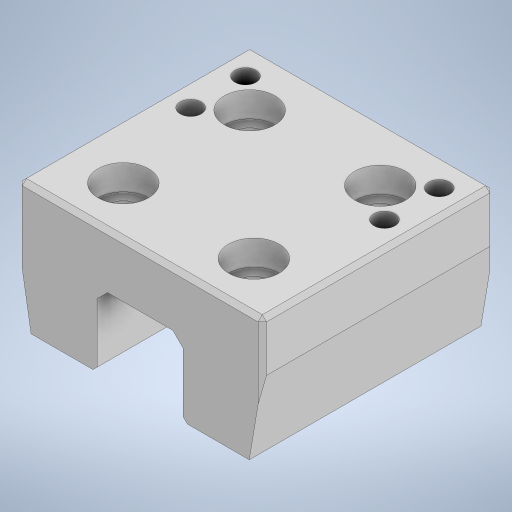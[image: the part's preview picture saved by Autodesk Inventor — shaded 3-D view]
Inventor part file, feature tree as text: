
AUTODESK INVENTOR PART (.ipt)
format: ipt  version: 2023 (Build 270158000, 158)  size: 463,872 bytes
history: native  units: in
note: dims shown in document units (in); Inventor stores cm internally (conversion verified against a paired STEP export)
features: extrude x11, sketch x7, projected_geometry x3, chamfer x2, thicken_offset x1
ambient origin geometry x8: Origin, YZ Plane, XZ Plane, XY Plane, X Axis, Y Axis, Z Axis, Center Point
bodies: Solid1 (feature_tree)
feature tree (24):
  extrude  "Extrusion1"  Depth=2.3622in
  extrude  "Extrusion2"  Depth=0.0197in
  extrude  "Extrusion3"  Depth=0.0197in
  extrude  "Extrusion4"  Depth=0.1969in
  extrude  "Extrusion5"  Depth=2.7874in
  extrude  "Extrusion6"  Depth=2.1654in TaperAngle=0.0deg
  extrude  "Extrusion9"  Depth=0.3937in TaperAngle=0.0deg
  extrude  "Extrusion10"  Depth=0.3937in TaperAngle=0.0deg
  extrude  "Extrusion11"  Depth=0.1969in
  extrude  "Extrusion12"  Depth=0.1969in TaperAngle=0.0deg
  extrude  "Extrusion13"  Depth=0.1969in
  chamfer  "Chamfer2"  Distance=0.2362in
  thicken_offset  "Thicken1"
  chamfer  "Chamfer1"  Distance=1.3937in
  sketch  "Sketch4"  dims[d0=0.9843in d1=2.3622in]
  sketch  "Sketch5"  dims[d2=0.0197in d3=0.0197in]
  sketch  "Sketch8"  dims[d4=0.0197in d5=0.0197in]
  sketch  "Sketch10"  dims[d6=0.1969in d7=1.811in]
  projected_geometry  "Projected Loop1"
  sketch  "Sketch11"  dims[d8=0.5118in d9=2.7874in]
  sketch  "Sketch12"  dims[d10=2.1654in d11=1.3937in d12=0.0in]
  sketch  "Sketch13"  dims[d13=1.3937in d14=0.0in d15=0.3937in d16=0.1969in d17=0.0in d18=0.0in d19=0.3937in d20=1.1969in d21=0.0in d22=0.0in d27=0.3937in d28=0.0in d29=0.2687in d31=1.4375in d32=0.0in d34=0.4724in d35=0.2362in d36=0.0in d50=1.3937in d51=0.0394in d52=0.1181in d53=135.0deg d54=0.0787in d55=0.1358in d56=0.689in d57=0.2819in d58=0.0935in d59=0.0525in d60=0.0953in d61=0.3937in d63=0.3937in d64=0.0in d66=0.0394in d67=0.125in d68=0.374in d69=0.689in d70=90.0deg d71=90.0deg d72=0.7874in d73=0.0394in d74=0.5315in d78=1.1811in d79=1.2205in d80=0.5315in d81=0.0787in d82=0.0787in d83=45.0deg d84=0.3937in d85=0.0in d86=2.2835in d88=0.0079in d89=0.0079in d90=0.002in d91=0.3937in d92=0.0in d93=0.1969in d94=0.0in d95=0.0in d96=0.1969in d97=0.0in d98=0.0394in d99=0.0787in d100=45.0deg d101=0.4724in d102=45.0deg d103=0.0965in]
  projected_geometry  "Projected Loop2"
  projected_geometry  "Projected Loop3"
